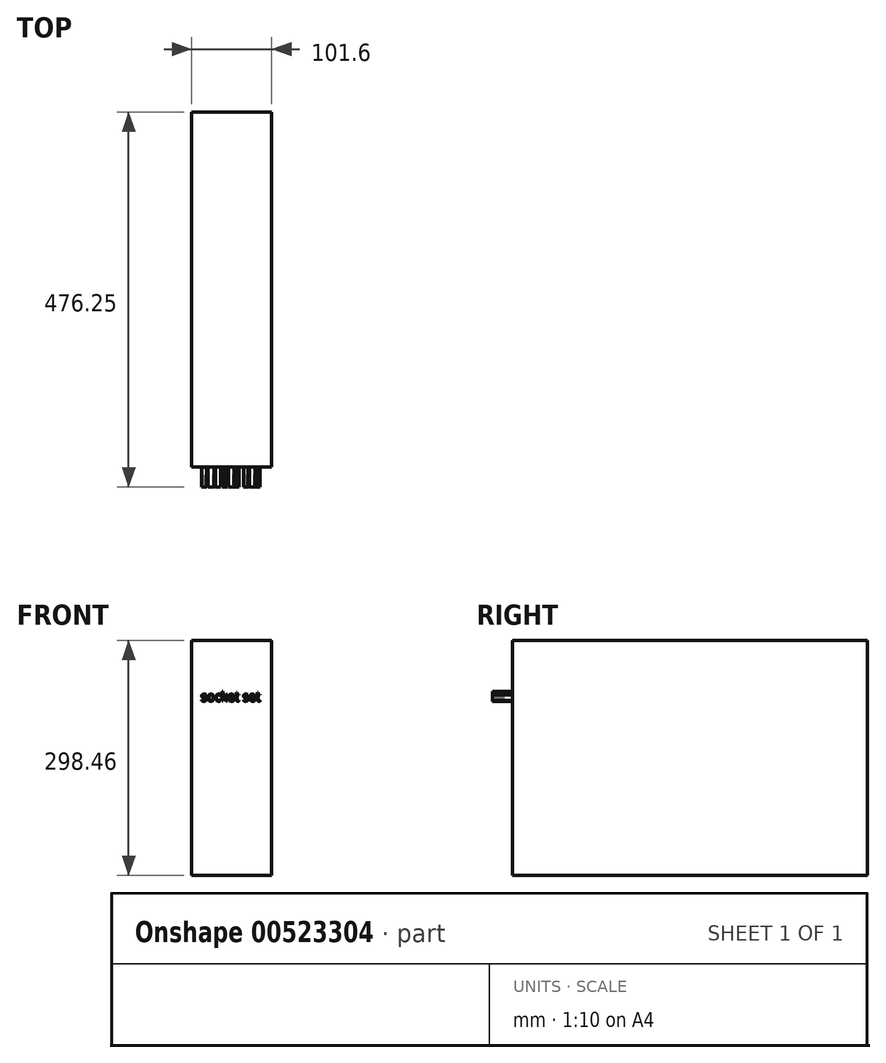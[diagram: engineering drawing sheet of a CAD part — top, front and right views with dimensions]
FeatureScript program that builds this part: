
annotation { "Feature Type Name" : "Feature", "Feature Type Description" : "" }
export const myFeature = defineFeature(function(context is Context, id is Id, definition is map)
    precondition{}
    {
        {
            var Q0;
            Q0=qCreatedBy(makeId("Front.planeOp"),FACE);
            var sketch = newSketch(context, id + "F0", { "sketchPlane" : qUnion([Q0])});
            skLineSegment(sketch, "E0.bottom", {"start": v(50.8, 149.23) * mm, "end": v(-50.8, 149.23) * mm});
            skLineSegment(sketch, "E0.top", {"start": v(50.8, -149.23) * mm, "end": v(-50.8, -149.23) * mm});
            skLineSegment(sketch, "E0.left", {"start": v(50.8, 149.23) * mm, "end": v(50.8, -149.23) * mm});
            skLineSegment(sketch, "E0.right", {"start": v(-50.8, 149.23) * mm, "end": v(-50.8, -149.23) * mm});
            skPoint(sketch, "E0.middle", {"position": v(0, 0) * mm});
            skSolve(sketch);
        }
        {
            var Q0;
            Q0=makeQuery(id+"F0.imprint","IMPRINT",FACE,{"disambiguationData":[TD([[makeQuery(id+"F0.imprint","IMPRINT",EDGE,{"derivedFrom":sQuery(id+"F0.wireOp",EDGE,"E0.bottom")}),1.0]])]});
            extrude(context, id + "F1", {"entities" : qUnion([Q0]), "depth" : 450.85 * mm, "offsetDistance" : 25.4 * mm});
        }
        {
            var Q0;
            Q0=makeQuery(id+"F1.opExtrude","CAP_FACE",FACE,{"disambiguationData":[OSD([sQuery(id+"F0.wireOp",EDGE,"E0.bottom"),sQuery(id+"F0.wireOp",EDGE,"E0.top"),sQuery(id+"F0.wireOp",EDGE,"E0.left"),sQuery(id+"F0.wireOp",EDGE,"E0.right")])],"isStart":false});
            var sketch = newSketch(context, id + "F2", { "sketchPlane" : qUnion([Q0])});
            skText(sketch, "E1", { "text": "socket set", "fontName": "OpenSans-Regular.ttf"});
            const initialGuessF2  = {"E1": [-0.03912, 0.07225, 1, 0, 0.0117]};
            skSetInitialGuess(sketch, initialGuessF2);
            skSolve(sketch);
        }
        {
            var Q0;
            Q0 = qSketchRegion(id + "F2", true);
            extrude(context, id + "F3", {"entities" : qUnion([Q0]), "operationType" : NewBodyOperationType.ADD, "depth" : 25.4 * mm, "offsetDistance" : 25.4 * mm});
        }
    });
